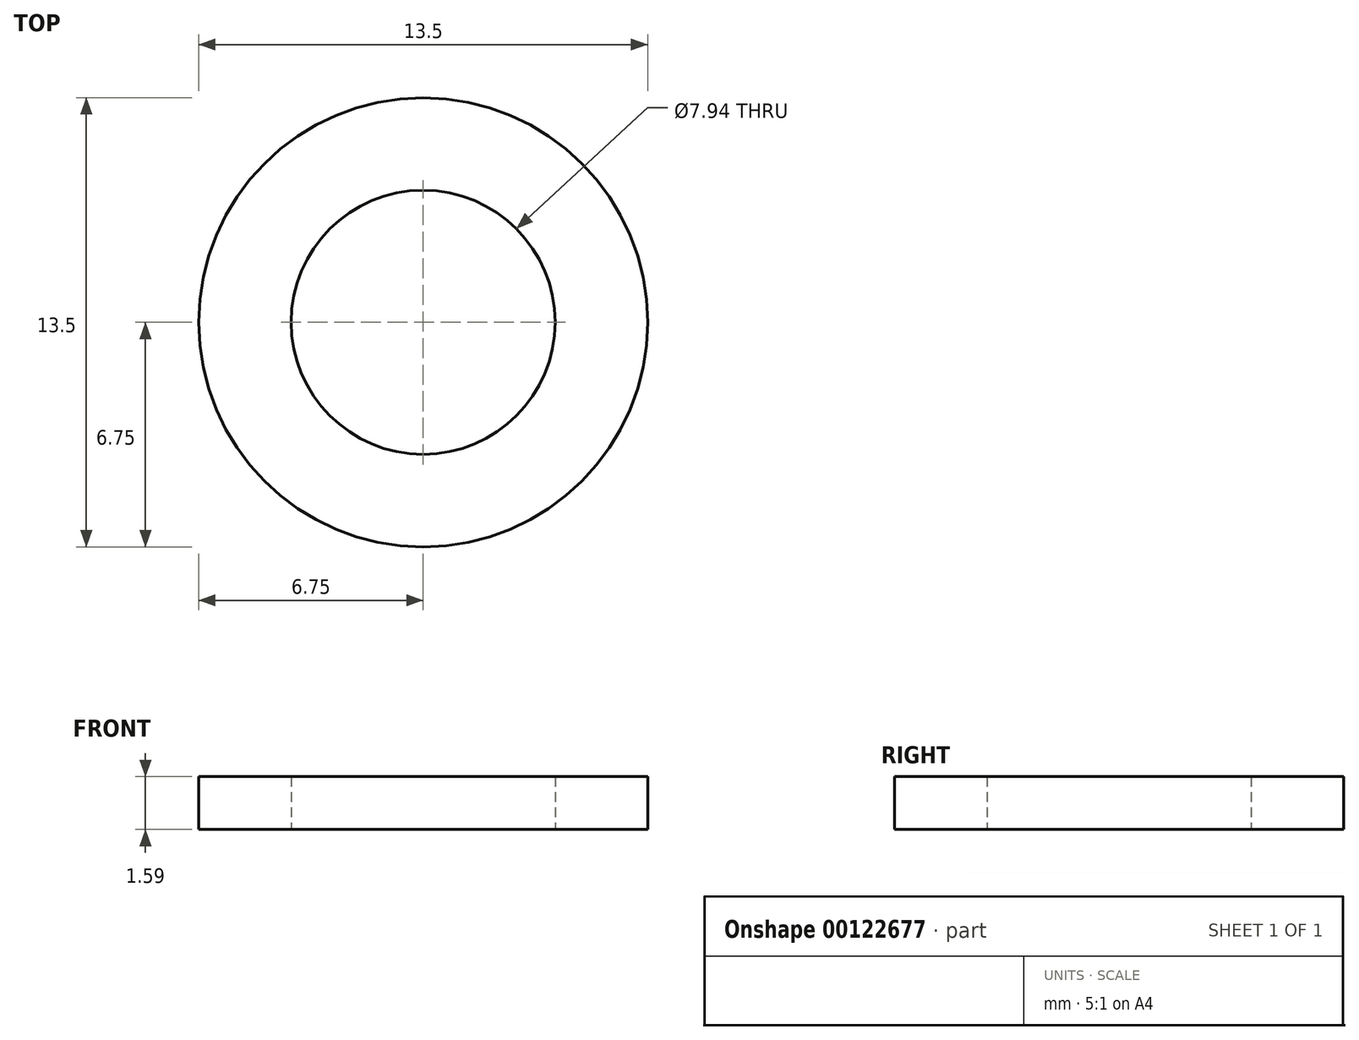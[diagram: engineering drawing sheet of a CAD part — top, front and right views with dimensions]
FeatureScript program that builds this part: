
annotation { "Feature Type Name" : "Feature", "Feature Type Description" : "" }
export const myFeature = defineFeature(function(context is Context, id is Id, definition is map)
    precondition{}
    {
        {
            var Q0;
            Q0=qCreatedBy(makeId("Top.planeOp"),FACE);
            var sketch = newSketch(context, id + "F0", { "sketchPlane" : qUnion([Q0])});
            skCircle(sketch, "E0", {"center": v(0, 0) * mm, "radius": 6.75 * mm});
            skCircle(sketch, "E1", {"center": v(0, 0) * mm, "radius": 3.97 * mm});
            skSolve(sketch);
        }
        {
            var Q0;
            Q0=makeQuery(id+"F0.imprint","IMPRINT",FACE,{"disambiguationData":[TD([[makeQuery(id+"F0.imprint","IMPRINT",EDGE,{"derivedFrom":sQuery(id+"F0.wireOp",EDGE,"E0")}),1.0]])]});
            extrude(context, id + "F1", {"entities" : qUnion([Q0]), "depth" : 1.59 * mm});
        }
    });
